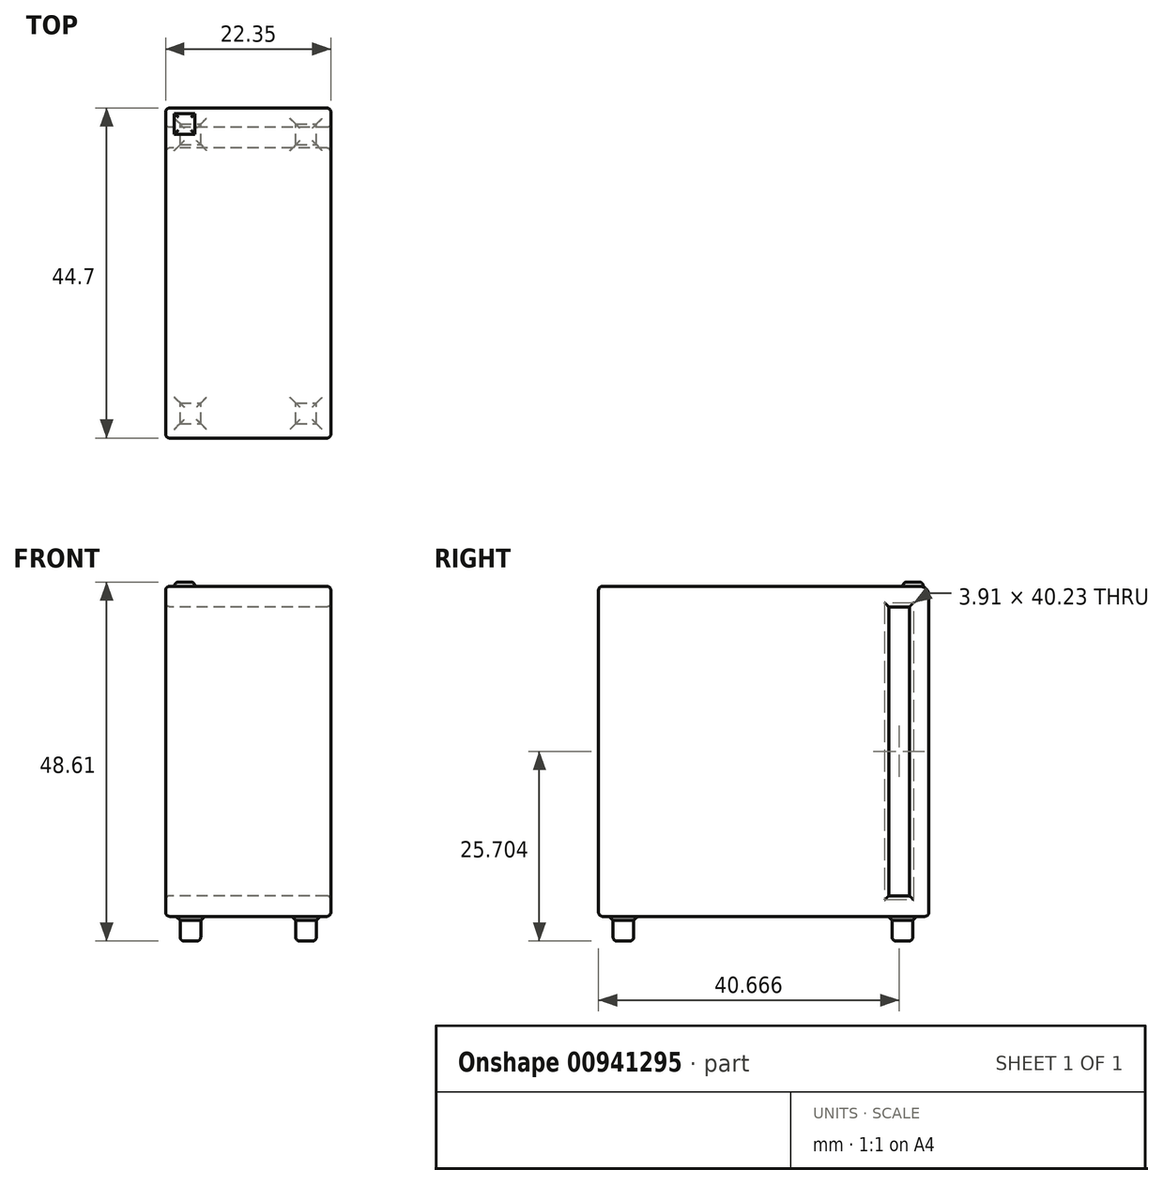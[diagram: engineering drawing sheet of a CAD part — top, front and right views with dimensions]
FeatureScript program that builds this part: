
annotation { "Feature Type Name" : "Feature", "Feature Type Description" : "" }
export const myFeature = defineFeature(function(context is Context, id is Id, definition is map)
    precondition{}
    {
        {
            var Q0;
            Q0=qCreatedBy(makeId("Front.planeOp"),FACE);
            var sketch = newSketch(context, id + "F0", { "sketchPlane" : qUnion([Q0])});
            skLineSegment(sketch, "E0.bottom", {"start": v(-102.64, 282.87) * mm, "end": v(100.56, 282.87) * mm});
            skLineSegment(sketch, "E0.top", {"start": v(-102.64, -123.53) * mm, "end": v(100.56, -123.53) * mm});
            skLineSegment(sketch, "E0.left", {"start": v(-102.64, 282.87) * mm, "end": v(-102.64, -123.53) * mm});
            skLineSegment(sketch, "E0.right", {"start": v(100.56, 282.87) * mm, "end": v(100.56, -123.53) * mm});
            skSolve(sketch);
        }
        {
            var Q0;
            Q0=makeQuery(id+"F0.imprint","IMPRINT",FACE,{"disambiguationData":[TD([[makeQuery(id+"F0.imprint","IMPRINT",EDGE,{"derivedFrom":sQuery(id+"F0.wireOp",EDGE,"E0.bottom")}),-1.0]])]});
            extrude(context, id + "F1", {"entities" : qUnion([Q0]), "depth" : 406.4 * mm, "offsetDistance" : 25.4 * mm});
        }
        {
            var Q0;
            Q0=makeQuery(id+"F1.opExtrude","SWEPT_FACE",FACE,{"disambiguationData":[OSD([sQuery(id+"F0.wireOp",EDGE,"E0.left")])]});
            var sketch = newSketch(context, id + "F2", { "sketchPlane" : qUnion([Q0])});
            skLineSegment(sketch, "E1.bottom", {"start": v(23.98, 257.47) * mm, "end": v(49.38, 257.47) * mm});
            skLineSegment(sketch, "E1.top", {"start": v(23.98, -98.13) * mm, "end": v(49.38, -98.13) * mm});
            skLineSegment(sketch, "E1.left", {"start": v(23.98, 257.47) * mm, "end": v(23.98, -98.13) * mm});
            skLineSegment(sketch, "E1.right", {"start": v(49.38, 257.47) * mm, "end": v(49.38, -98.13) * mm});
            skSolve(sketch);
        }
        {
            var Q0;
            Q0=makeQuery(id+"F2.imprint","IMPRINT",FACE,{"disambiguationData":[TD([[makeQuery(id+"F2.imprint","IMPRINT",EDGE,{"derivedFrom":sQuery(id+"F2.wireOp",EDGE,"E1.bottom")}),-1.0]])]});
            extrude(context, id + "F3", {"entities" : qUnion([Q0]), "operationType" : NewBodyOperationType.REMOVE, "endBound" : BoundingType.THROUGH_ALL, "oppositeDirection" : true, "depth" : 25.4 * mm, "offsetDistance" : 25.4 * mm});
        }
        {
            var Q0;
            Q0=makeQuery(id+"F1.opExtrude","SWEPT_FACE",FACE,{"disambiguationData":[OSD([sQuery(id+"F0.wireOp",EDGE,"E0.bottom")])]});
            var sketch = newSketch(context, id + "F4", { "sketchPlane" : qUnion([Q0])});
            skLineSegment(sketch, "E2.bottom", {"start": v(-91.89, -6.8) * mm, "end": v(-66.49, -6.8) * mm});
            skLineSegment(sketch, "E2.top", {"start": v(-91.89, -32.2) * mm, "end": v(-66.49, -32.2) * mm});
            skLineSegment(sketch, "E2.left", {"start": v(-91.89, -6.8) * mm, "end": v(-91.89, -32.2) * mm});
            skLineSegment(sketch, "E2.right", {"start": v(-66.49, -6.8) * mm, "end": v(-66.49, -32.2) * mm});
            skSolve(sketch);
        }
        {
            var Q0;
            Q0=makeQuery(id+"F4.imprint","IMPRINT",FACE,{"disambiguationData":[TD([[makeQuery(id+"F4.imprint","IMPRINT",EDGE,{"derivedFrom":sQuery(id+"F4.wireOp",EDGE,"E2.bottom")}),-1.0]])]});
            extrude(context, id + "F5", {"entities" : qUnion([Q0]), "operationType" : NewBodyOperationType.ADD, "depth" : 5.08 * mm, "offsetDistance" : 25.4 * mm});
        }
        {
            var Q0;
            Q0=makeQuery(id+"F1.opExtrude","SWEPT_FACE",FACE,{"disambiguationData":[OSD([sQuery(id+"F0.wireOp",EDGE,"E0.right")])]});
            var Q1;
            Q1=makeQuery(id+"F1.opExtrude","SWEPT_FACE",FACE,{"disambiguationData":[OSD([sQuery(id+"F0.wireOp",EDGE,"E0.left")])]});
            fillet(context, id + "F6", {"entities" : qUnion([Q0, Q1]), "radius" : 5.08 * mm, "tangentPropagation" : true, "allowEdgeOverflow" : false});
        }
        {
            var Q0;
            Q0=makeQuery(id+"F1.opExtrude","SWEPT_FACE",FACE,{"disambiguationData":[OSD([sQuery(id+"F0.wireOp",EDGE,"E0.top")])]});
            var Q1;
            Q1=makeQuery(id+"F5.opExtrude","CAP_FACE",FACE,{"disambiguationData":[OSD([sQuery(id+"F4.wireOp",EDGE,"E2.bottom"),sQuery(id+"F4.wireOp",EDGE,"E2.top"),sQuery(id+"F4.wireOp",EDGE,"E2.left"),sQuery(id+"F4.wireOp",EDGE,"E2.right")])],"isStart":false});
            fillet(context, id + "F7", {"entities" : qUnion([Q0, Q1]), "radius" : 5.08 * mm, "tangentPropagation" : true, "allowEdgeOverflow" : false});
        }
        {
            var Q0;
            Q0=makeQuery(id+"F1.opExtrude","CAP_EDGE",EDGE,{"disambiguationData":[OSD([sQuery(id+"F0.wireOp",EDGE,"E0.bottom")])],"isStart":false});
            fillet(context, id + "F8", {"entities" : qUnion([Q0]), "radius" : 5.08 * mm, "tangentPropagation" : true, "allowEdgeOverflow" : false});
        }
        {
            var Q0;
            Q0=makeQuery(id+"F1.opExtrude","SWEPT_FACE",FACE,{"disambiguationData":[OSD([sQuery(id+"F0.wireOp",EDGE,"E0.top")])]});
            var sketch = newSketch(context, id + "F9", { "sketchPlane" : qUnion([Q0])});
            skLineSegment(sketch, "E3.bottom", {"start": v(-84.86, 388.62) * mm, "end": v(-59.46, 388.62) * mm});
            skLineSegment(sketch, "E3.top", {"start": v(-84.86, 363.22) * mm, "end": v(-59.46, 363.22) * mm});
            skLineSegment(sketch, "E3.left", {"start": v(-84.86, 388.62) * mm, "end": v(-84.86, 363.22) * mm});
            skLineSegment(sketch, "E3.right", {"start": v(-59.46, 388.62) * mm, "end": v(-59.46, 363.22) * mm});
            skLineSegment(sketch, "E4.bottom", {"start": v(57.38, 388.62) * mm, "end": v(82.78, 388.62) * mm});
            skLineSegment(sketch, "E4.top", {"start": v(57.38, 363.22) * mm, "end": v(82.78, 363.22) * mm});
            skLineSegment(sketch, "E4.left", {"start": v(57.38, 388.62) * mm, "end": v(57.38, 363.22) * mm});
            skLineSegment(sketch, "E4.right", {"start": v(82.78, 388.62) * mm, "end": v(82.78, 363.22) * mm});
            skLineSegment(sketch, "E5.bottom", {"start": v(-84.86, 45.28) * mm, "end": v(-59.46, 45.28) * mm});
            skLineSegment(sketch, "E5.top", {"start": v(-84.86, 19.88) * mm, "end": v(-59.46, 19.88) * mm});
            skLineSegment(sketch, "E5.left", {"start": v(-84.86, 45.28) * mm, "end": v(-84.86, 19.88) * mm});
            skLineSegment(sketch, "E5.right", {"start": v(-59.46, 45.28) * mm, "end": v(-59.46, 19.88) * mm});
            skLineSegment(sketch, "E6.bottom", {"start": v(57.38, 45.28) * mm, "end": v(82.78, 45.28) * mm});
            skLineSegment(sketch, "E6.top", {"start": v(57.38, 19.88) * mm, "end": v(82.78, 19.88) * mm});
            skLineSegment(sketch, "E6.left", {"start": v(57.38, 45.28) * mm, "end": v(57.38, 19.88) * mm});
            skLineSegment(sketch, "E6.right", {"start": v(82.78, 45.28) * mm, "end": v(82.78, 19.88) * mm});
            skLineSegment(sketch, "E7", {"start": v(-1.04, -43.62) * mm, "end": v(-1.04, 401.32) * mm});
            skPoint(sketch, "E8", {"position": v(-1.04, 178.85) * mm});
            skSolve(sketch);
        }
        {
            var Q0;
            Q0=makeQuery(id+"F9.imprint","IMPRINT",FACE,{"disambiguationData":[TD([[makeQuery(id+"F9.imprint","IMPRINT",EDGE,{"derivedFrom":sQuery(id+"F9.wireOp",EDGE,"E3.bottom")}),-1.0]])]});
            var Q1;
            Q1=makeQuery(id+"F9.imprint","IMPRINT",FACE,{"disambiguationData":[TD([[makeQuery(id+"F9.imprint","IMPRINT",EDGE,{"derivedFrom":sQuery(id+"F9.wireOp",EDGE,"E4.bottom")}),-1.0]])]});
            var Q2;
            Q2=makeQuery(id+"F9.imprint","IMPRINT",FACE,{"disambiguationData":[TD([[makeQuery(id+"F9.imprint","IMPRINT",EDGE,{"derivedFrom":sQuery(id+"F9.wireOp",EDGE,"E6.bottom")}),-1.0]])]});
            var Q3;
            Q3=makeQuery(id+"F9.imprint","IMPRINT",FACE,{"disambiguationData":[TD([[makeQuery(id+"F9.imprint","IMPRINT",EDGE,{"derivedFrom":sQuery(id+"F9.wireOp",EDGE,"E5.bottom")}),-1.0]])]});
            extrude(context, id + "F10", {"entities" : qUnion([Q0, Q1, Q2, Q3]), "operationType" : NewBodyOperationType.ADD, "depth" : 30.48 * mm, "offsetDistance" : 25.4 * mm});
        }
        {
            var Q0;
            Q0=makeQuery(id+"F1.opExtrude","SWEPT_FACE",FACE,{"disambiguationData":[OSD([sQuery(id+"F0.wireOp",EDGE,"E0.top")])]});
            chamfer(context, id + "F11", {"entities" : qUnion([Q0]), "width" : 5.08 * mm, "tangentPropagation" : true});
        }
        {
            var Q0;
            Q0=makeQuery(id+"F10.opExtrude","CAP_FACE",FACE,{"disambiguationData":[OSD([sQuery(id+"F9.wireOp",EDGE,"E5.bottom"),sQuery(id+"F9.wireOp",EDGE,"E5.top"),sQuery(id+"F9.wireOp",EDGE,"E5.left"),sQuery(id+"F9.wireOp",EDGE,"E5.right")])],"isStart":false});
            var Q1;
            Q1=makeQuery(id+"F10.opExtrude","CAP_FACE",FACE,{"disambiguationData":[OSD([sQuery(id+"F9.wireOp",EDGE,"E6.bottom"),sQuery(id+"F9.wireOp",EDGE,"E6.top"),sQuery(id+"F9.wireOp",EDGE,"E6.left"),sQuery(id+"F9.wireOp",EDGE,"E6.right")])],"isStart":false});
            var Q2;
            Q2=makeQuery(id+"F10.opExtrude","CAP_FACE",FACE,{"disambiguationData":[OSD([sQuery(id+"F9.wireOp",EDGE,"E4.bottom"),sQuery(id+"F9.wireOp",EDGE,"E4.top"),sQuery(id+"F9.wireOp",EDGE,"E4.left"),sQuery(id+"F9.wireOp",EDGE,"E4.right")])],"isStart":false});
            var Q3;
            Q3=makeQuery(id+"F10.opExtrude","CAP_FACE",FACE,{"disambiguationData":[OSD([sQuery(id+"F9.wireOp",EDGE,"E3.bottom"),sQuery(id+"F9.wireOp",EDGE,"E3.top"),sQuery(id+"F9.wireOp",EDGE,"E3.left"),sQuery(id+"F9.wireOp",EDGE,"E3.right")])],"isStart":false});
            var Q4;
            Q4=makeQuery(id+"F1.opExtrude","SWEPT_FACE",FACE,{"disambiguationData":[OSD([sQuery(id+"F0.wireOp",EDGE,"E0.top")])]});
            fillet(context, id + "F12", {"entities" : qUnion([Q0, Q1, Q2, Q3, Q4]), "radius" : 5.08 * mm, "tangentPropagation" : true, "allowEdgeOverflow" : false});
        }
        {
            var Q0;
            Q0=makeQuery(id+"F1.opExtrude","SWEPT_BODY",BODY,{"disambiguationData":[OSD([sQuery(id+"F0.wireOp",EDGE,"E0.bottom"),sQuery(id+"F0.wireOp",EDGE,"E0.top"),sQuery(id+"F0.wireOp",EDGE,"E0.left"),sQuery(id+"F0.wireOp",EDGE,"E0.right")])]});
            var Q1;
            Q1=qCreatedBy(makeId("Origin.pointOp"),VERTEX);
            transform(context, id + "F13", {"entities" : qUnion([Q0]), "transformType" : TransformType.SCALE_UNIFORMLY, "scale" : .11, "scalePoint" : qUnion([Q1]), "makeCopy" : false});
        }
        {
            var Q0;
            Q0=makeQuery(id+"F1.opExtrude","CAP_EDGE",EDGE,{"disambiguationData":[OSD([sQuery(id+"F0.wireOp",EDGE,"E0.bottom")])],"isStart":true});
            fillet(context, id + "F14", {"entities" : qUnion([Q0]), "radius" : 1.27 * mm, "tangentPropagation" : true, "allowEdgeOverflow" : false});
        }
    });
